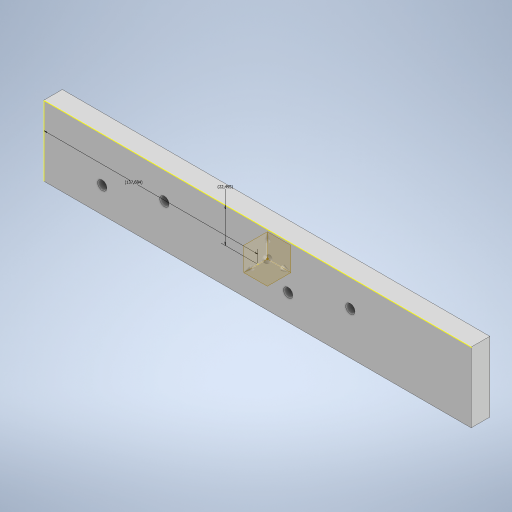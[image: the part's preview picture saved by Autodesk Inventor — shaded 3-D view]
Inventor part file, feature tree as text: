
AUTODESK INVENTOR PART (.ipt)
format: ipt  version: 2024 (Build 280153000, 153)  size: 239,616 bytes
history: native  units: mm
features: other x6, sketch x1
ambient origin geometry x8: Origin, YZ Plane, XZ Plane, XY Plane, X Axis, Y Axis, Z Axis, Center Point
bodies: Body1 (feature_tree)
feature tree (7):
  other  "BORDE_4"
  other  "Generador_de_Piezas.ipt"
  other  "Desplazar cuerpo1"
  sketch  "Boceto1"  dims[d0=10.0mm d1=-462.937mm d2=-2337.776mm d3=0.0mm d4=22.494936mm d5=137.68417mm d6=-0.184mm d7=-0.005mm d8=0.0mm]
  other  "Desplazar cuerpo2"
  other  "BORDE_4::Generador_de_Piezas.ipt"
  other  "OperaciónIdentificador1"
